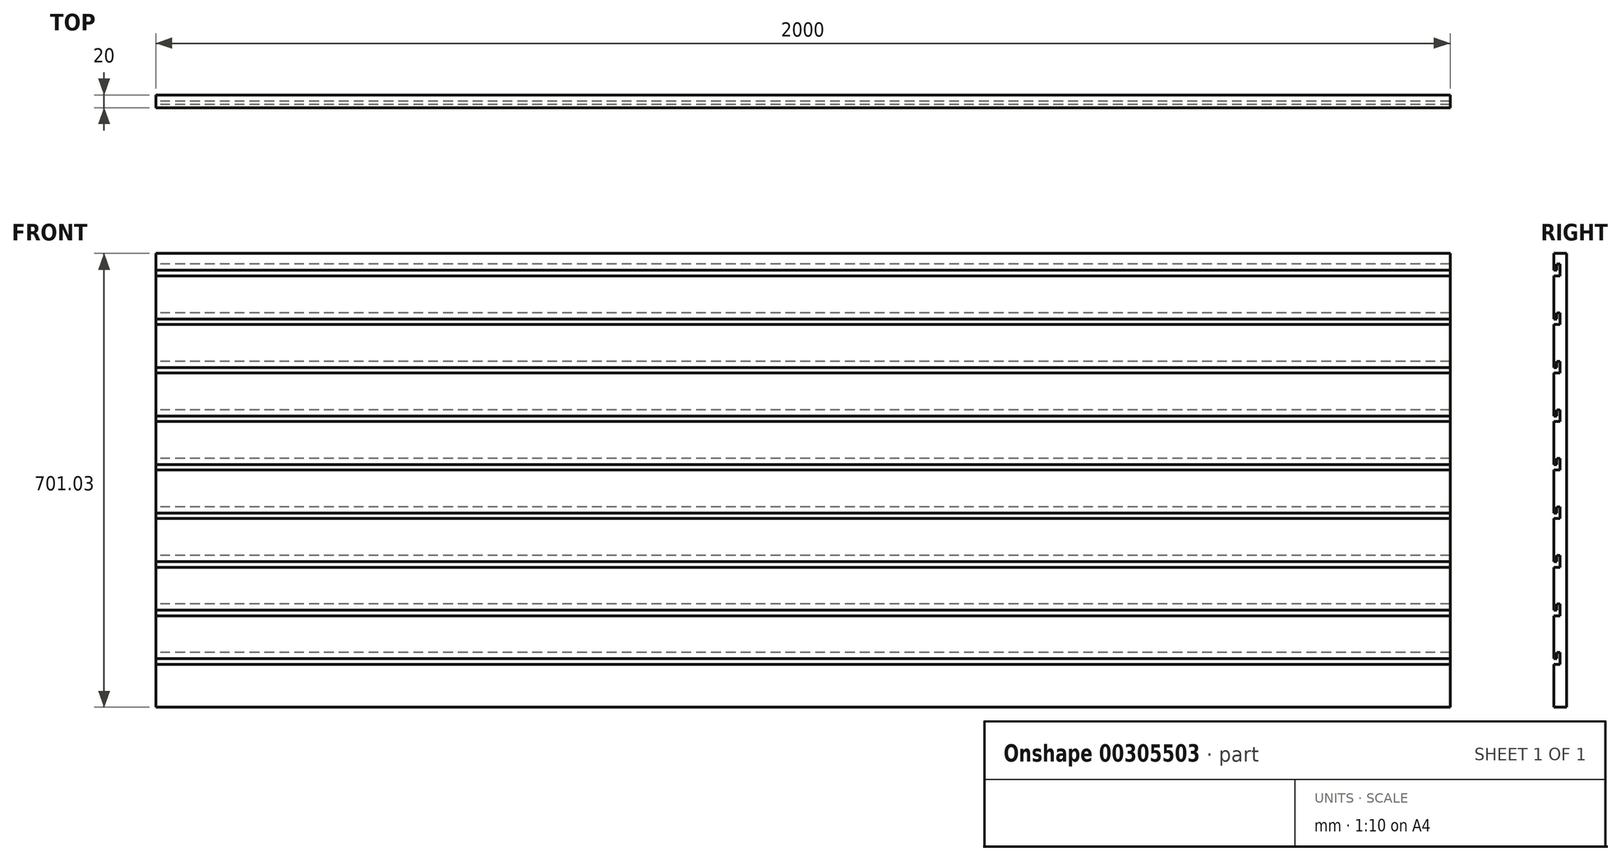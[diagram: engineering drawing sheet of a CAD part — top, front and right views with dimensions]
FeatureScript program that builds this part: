
annotation { "Feature Type Name" : "Feature", "Feature Type Description" : "" }
export const myFeature = defineFeature(function(context is Context, id is Id, definition is map)
    precondition{}
    {
        {
            var Q0;
            Q0=qCreatedBy(makeId("Right.planeOp"),FACE);
            var sketch = newSketch(context, id + "F0", { "sketchPlane" : qUnion([Q0])});
            skLineSegment(sketch, "E0", {"start": v(0, 0) * mm, "end": v(0, 66.5) * mm});
            skLineSegment(sketch, "E1", {"start": v(0, 66.5) * mm, "end": v(10, 66.5) * mm});
            skLineSegment(sketch, "E2", {"start": v(10, 66.5) * mm, "end": v(10, 84.5) * mm});
            skLineSegment(sketch, "E3", {"start": v(10, 84.5) * mm, "end": v(5, 84.5) * mm});
            skLineSegment(sketch, "E4", {"start": v(5, 84.5) * mm, "end": v(5, 75) * mm});
            skLineSegment(sketch, "E5", {"start": v(5, 75) * mm, "end": v(0, 75) * mm});
            skLineSegment(sketch, "E6.0.1.0", {"start": v(5, 9.5) * mm, "end": v(5, 0) * mm});
            skLineSegment(sketch, "E6.0.1.1", {"start": v(10, -8.5) * mm, "end": v(10, 9.5) * mm});
            skLineSegment(sketch, "E6.0.1.2", {"start": v(0, -8.5) * mm, "end": v(10, -8.5) * mm});
            skLineSegment(sketch, "E6.0.1.3", {"start": v(0, -75) * mm, "end": v(0, -8.5) * mm});
            skLineSegment(sketch, "E6.0.1.4", {"start": v(5, 0) * mm, "end": v(0, 0) * mm});
            skLineSegment(sketch, "E6.0.1.5", {"start": v(10, 9.5) * mm, "end": v(5, 9.5) * mm});
            skLineSegment(sketch, "E6.0.2.0", {"start": v(5, -65.5) * mm, "end": v(5, -75) * mm});
            skLineSegment(sketch, "E6.0.2.1", {"start": v(10, -83.5) * mm, "end": v(10, -65.5) * mm});
            skLineSegment(sketch, "E6.0.2.2", {"start": v(0, -83.5) * mm, "end": v(10, -83.5) * mm});
            skLineSegment(sketch, "E6.0.2.3", {"start": v(0, -150) * mm, "end": v(0, -83.5) * mm});
            skLineSegment(sketch, "E6.0.2.4", {"start": v(5, -75) * mm, "end": v(0, -75) * mm});
            skLineSegment(sketch, "E6.0.2.5", {"start": v(10, -65.5) * mm, "end": v(5, -65.5) * mm});
            skLineSegment(sketch, "E6.0.3.0", {"start": v(5, -140.5) * mm, "end": v(5, -150) * mm});
            skLineSegment(sketch, "E6.0.3.1", {"start": v(10, -158.5) * mm, "end": v(10, -140.5) * mm});
            skLineSegment(sketch, "E6.0.3.2", {"start": v(0, -158.5) * mm, "end": v(10, -158.5) * mm});
            skLineSegment(sketch, "E6.0.3.3", {"start": v(0, -225) * mm, "end": v(0, -158.5) * mm});
            skLineSegment(sketch, "E6.0.3.4", {"start": v(5, -150) * mm, "end": v(0, -150) * mm});
            skLineSegment(sketch, "E6.0.3.5", {"start": v(10, -140.5) * mm, "end": v(5, -140.5) * mm});
            skLineSegment(sketch, "E6.0.4.0", {"start": v(5, -215.5) * mm, "end": v(5, -225) * mm});
            skLineSegment(sketch, "E6.0.4.1", {"start": v(10, -233.5) * mm, "end": v(10, -215.5) * mm});
            skLineSegment(sketch, "E6.0.4.2", {"start": v(0, -233.5) * mm, "end": v(10, -233.5) * mm});
            skLineSegment(sketch, "E6.0.4.3", {"start": v(0, -300) * mm, "end": v(0, -233.5) * mm});
            skLineSegment(sketch, "E6.0.4.4", {"start": v(5, -225) * mm, "end": v(0, -225) * mm});
            skLineSegment(sketch, "E6.0.4.5", {"start": v(10, -215.5) * mm, "end": v(5, -215.5) * mm});
            skLineSegment(sketch, "E6.0.5.0", {"start": v(5, -290.5) * mm, "end": v(5, -300) * mm});
            skLineSegment(sketch, "E6.0.5.1", {"start": v(10, -308.5) * mm, "end": v(10, -290.5) * mm});
            skLineSegment(sketch, "E6.0.5.2", {"start": v(0, -308.5) * mm, "end": v(10, -308.5) * mm});
            skLineSegment(sketch, "E6.0.5.3", {"start": v(0, -375) * mm, "end": v(0, -308.5) * mm});
            skLineSegment(sketch, "E6.0.5.4", {"start": v(5, -300) * mm, "end": v(0, -300) * mm});
            skLineSegment(sketch, "E6.0.5.5", {"start": v(10, -290.5) * mm, "end": v(5, -290.5) * mm});
            skLineSegment(sketch, "E6.0.6.0", {"start": v(5, -365.5) * mm, "end": v(5, -375) * mm});
            skLineSegment(sketch, "E6.0.6.1", {"start": v(10, -383.5) * mm, "end": v(10, -365.5) * mm});
            skLineSegment(sketch, "E6.0.6.2", {"start": v(0, -383.5) * mm, "end": v(10, -383.5) * mm});
            skLineSegment(sketch, "E6.0.6.3", {"start": v(0, -450) * mm, "end": v(0, -383.5) * mm});
            skLineSegment(sketch, "E6.0.6.4", {"start": v(5, -375) * mm, "end": v(0, -375) * mm});
            skLineSegment(sketch, "E6.0.6.5", {"start": v(10, -365.5) * mm, "end": v(5, -365.5) * mm});
            skLineSegment(sketch, "E6.0.7.0", {"start": v(5, -440.5) * mm, "end": v(5, -450) * mm});
            skLineSegment(sketch, "E6.0.7.1", {"start": v(10, -458.5) * mm, "end": v(10, -440.5) * mm});
            skLineSegment(sketch, "E6.0.7.2", {"start": v(0, -458.5) * mm, "end": v(10, -458.5) * mm});
            skLineSegment(sketch, "E6.0.7.3", {"start": v(0, -525) * mm, "end": v(0, -458.5) * mm});
            skLineSegment(sketch, "E6.0.7.4", {"start": v(5, -450) * mm, "end": v(0, -450) * mm});
            skLineSegment(sketch, "E6.0.7.5", {"start": v(10, -440.5) * mm, "end": v(5, -440.5) * mm});
            skLineSegment(sketch, "E6.0.8.0", {"start": v(5, -515.5) * mm, "end": v(5, -525) * mm});
            skLineSegment(sketch, "E6.0.8.1", {"start": v(10, -533.5) * mm, "end": v(10, -515.5) * mm});
            skLineSegment(sketch, "E6.0.8.2", {"start": v(0, -533.5) * mm, "end": v(10, -533.5) * mm});
            skLineSegment(sketch, "E6.0.8.3", {"start": v(0, -600) * mm, "end": v(0, -533.5) * mm});
            skLineSegment(sketch, "E6.0.8.4", {"start": v(5, -525) * mm, "end": v(0, -525) * mm});
            skLineSegment(sketch, "E6.0.8.5", {"start": v(10, -515.5) * mm, "end": v(5, -515.5) * mm});
            skLineSegment(sketch, "E6.direction1", {"start": v(0, 0) * mm, "end": v(25, 0) * mm, "construction": true});
            skLineSegment(sketch, "E6.direction2", {"start": v(0, 0) * mm, "end": v(0, -75) * mm, "construction": true});
            skLineSegment(sketch, "E7", {"start": v(0, 75) * mm, "end": v(0, 101.03) * mm});
            skLineSegment(sketch, "E8", {"start": v(0, 101.03) * mm, "end": v(20, 101.03) * mm});
            skLineSegment(sketch, "E9", {"start": v(20, 101.03) * mm, "end": v(20, -600) * mm});
            skLineSegment(sketch, "E10", {"start": v(0, -600) * mm, "end": v(20, -600) * mm});
            skSolve(sketch);
        }
        {
            var Q0;
            Q0=makeQuery(id+"F0.imprint","IMPRINT",FACE,{"disambiguationData":[TD([[makeQuery(id+"F0.imprint","IMPRINT",EDGE,{"derivedFrom":sQuery(id+"F0.wireOp",EDGE,"E0")}),-1.0]])]});
            extrude(context, id + "F1", {"entities" : qUnion([Q0]), "endBound" : BoundingType.SYMMETRIC, "depth" : 2000 * mm});
        }
    });
